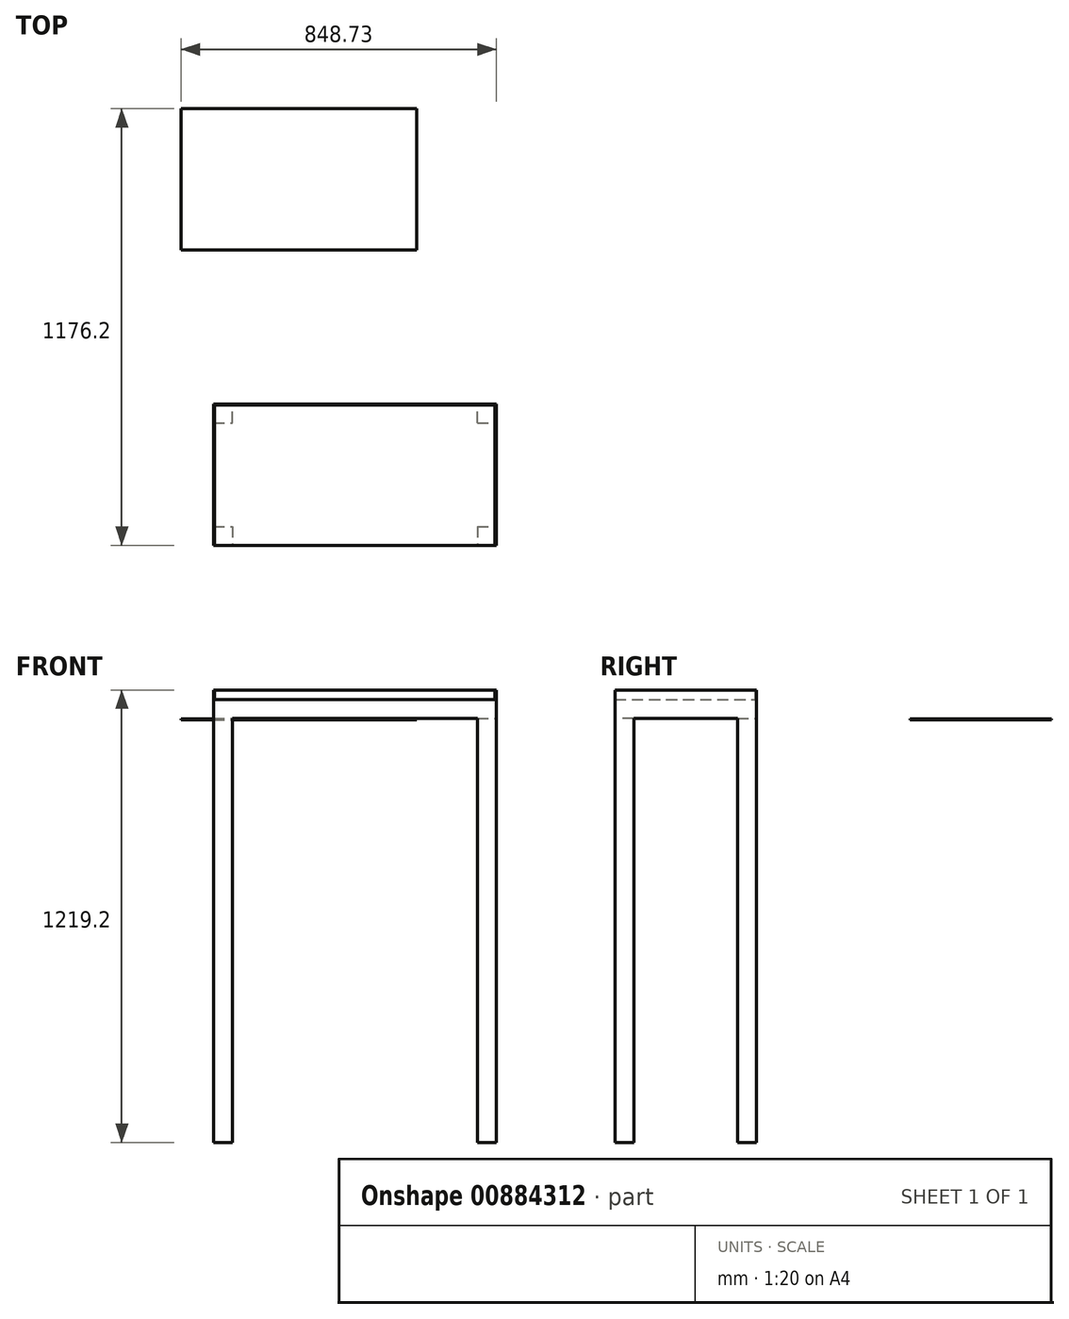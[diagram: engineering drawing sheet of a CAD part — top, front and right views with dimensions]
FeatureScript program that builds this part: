
annotation { "Feature Type Name" : "Feature", "Feature Type Description" : "" }
export const myFeature = defineFeature(function(context is Context, id is Id, definition is map)
    precondition{}
    {
        {
            var Q0;
            Q0=qCreatedBy(makeId("Front.planeOp"),FACE);
            var sketch = newSketch(context, id + "F0", { "sketchPlane" : qUnion([Q0])});
            skLineSegment(sketch, "E0.bottom", {"start": v(-294.8, 52.32) * mm, "end": v(467.2, 52.32) * mm});
            skLineSegment(sketch, "E0.top", {"start": v(-294.8, 1.52) * mm, "end": v(467.2, 1.52) * mm});
            skLineSegment(sketch, "E0.left", {"start": v(-294.8, 52.32) * mm, "end": v(-294.8, 1.52) * mm});
            skLineSegment(sketch, "E0.right", {"start": v(467.2, 52.32) * mm, "end": v(467.2, 1.52) * mm});
            skSolve(sketch);
        }
        {
            var Q0;
            Q0=makeQuery(id+"F0.imprint","IMPRINT",FACE,{"disambiguationData":[TD([[makeQuery(id+"F0.imprint","IMPRINT",EDGE,{"derivedFrom":sQuery(id+"F0.wireOp",EDGE,"E0.bottom")}),-1.0]])]});
            extrude(context, id + "F1", {"entities" : qUnion([Q0]), "depth" : 381 * mm, "offsetDistance" : 25.4 * mm});
        }
        {
            var Q0;
            Q0=makeQuery(id+"F1.opExtrude","CAP_FACE",FACE,{"disambiguationData":[OSD([sQuery(id+"F0.wireOp",EDGE,"E0.bottom"),sQuery(id+"F0.wireOp",EDGE,"E0.top"),sQuery(id+"F0.wireOp",EDGE,"E0.left"),sQuery(id+"F0.wireOp",EDGE,"E0.right")])],"isStart":false});
            var sketch = newSketch(context, id + "F2", { "sketchPlane" : qUnion([Q0])});
            skLineSegment(sketch, "E1", {"start": v(-294.8, 1.52) * mm, "end": v(-294.8, -1141.48) * mm});
            skLineSegment(sketch, "E2", {"start": v(-294.8, -1141.48) * mm, "end": v(-244, -1141.48) * mm});
            skLineSegment(sketch, "E3", {"start": v(-244, -1141.48) * mm, "end": v(-244, 1.52) * mm});
            skLineSegment(sketch, "E4", {"start": v(467.2, 1.52) * mm, "end": v(467.2, -1141.48) * mm});
            skLineSegment(sketch, "E5", {"start": v(467.2, -1141.48) * mm, "end": v(416.4, -1141.48) * mm});
            skLineSegment(sketch, "E6", {"start": v(416.4, -1141.48) * mm, "end": v(416.4, 1.52) * mm});
            skSolve(sketch);
        }
        {
            var Q0;
            {var subQ0=sQuery(id+"F2.wireOp",EDGE,"E1");Q0=makeQuery(id+"F2.imprint","IMPRINT",FACE,{"disambiguationData":[TD([[makeQuery(id+"F2.imprint","IMPRINT",EDGE,{"derivedFrom":subQ0}),1.0]])]});}
            var Q1;
            {var subQ0=sQuery(id+"F2.wireOp",EDGE,"E4");Q1=makeQuery(id+"F2.imprint","IMPRINT",FACE,{"disambiguationData":[TD([[makeQuery(id+"F2.imprint","IMPRINT",EDGE,{"derivedFrom":subQ0}),-1.0]])]});}
            extrude(context, id + "F3", {"entities" : qUnion([Q0, Q1]), "operationType" : NewBodyOperationType.ADD, "depth" : -50.8 * mm, "offsetDistance" : 25.4 * mm});
        }
        {
            var Q0;
            Q0=makeQuery(id+"F1.opExtrude","CAP_FACE",FACE,{"disambiguationData":[OSD([sQuery(id+"F0.wireOp",EDGE,"E0.bottom"),sQuery(id+"F0.wireOp",EDGE,"E0.top"),sQuery(id+"F0.wireOp",EDGE,"E0.left"),sQuery(id+"F0.wireOp",EDGE,"E0.right")])],"isStart":true});
            var sketch = newSketch(context, id + "F4", { "sketchPlane" : qUnion([Q0])});
            skLineSegment(sketch, "E7", {"start": v(-467.2, 1.52) * mm, "end": v(-467.2, -1141.48) * mm});
            skLineSegment(sketch, "E8", {"start": v(-467.2, -1141.48) * mm, "end": v(-416.4, -1141.48) * mm});
            skLineSegment(sketch, "E9", {"start": v(-416.4, -1141.48) * mm, "end": v(-416.4, 1.52) * mm});
            skLineSegment(sketch, "E10", {"start": v(294.8, 1.52) * mm, "end": v(294.8, -1141.48) * mm});
            skLineSegment(sketch, "E11", {"start": v(294.8, -1141.48) * mm, "end": v(244, -1141.48) * mm});
            skLineSegment(sketch, "E12", {"start": v(244, -1141.48) * mm, "end": v(244, 1.52) * mm});
            skSolve(sketch);
        }
        {
            var Q0;
            {var subQ0=sQuery(id+"F4.wireOp",EDGE,"E7");Q0=makeQuery(id+"F4.imprint","IMPRINT",FACE,{"disambiguationData":[TD([[makeQuery(id+"F4.imprint","IMPRINT",EDGE,{"derivedFrom":subQ0}),1.0]])]});}
            var Q1;
            {var subQ0=sQuery(id+"F4.wireOp",EDGE,"E10");Q1=makeQuery(id+"F4.imprint","IMPRINT",FACE,{"disambiguationData":[TD([[makeQuery(id+"F4.imprint","IMPRINT",EDGE,{"derivedFrom":subQ0}),-1.0]])]});}
            extrude(context, id + "F5", {"entities" : qUnion([Q0, Q1]), "operationType" : NewBodyOperationType.ADD, "depth" : -50.8 * mm, "offsetDistance" : 25.4 * mm});
        }
        {
            var Q0;
            Q0=makeQuery(id+"F5.boolean.opBoolean","MERGE",FACE,{"derivedFrom":[makeQuery(id+"F3.boolean.opBoolean","MERGE",FACE,{"derivedFrom":[makeQuery(id+"F1.opExtrude","SWEPT_FACE",FACE,{"disambiguationData":[OSD([sQuery(id+"F0.wireOp",EDGE,"E0.right")])]}),makeQuery(id+"F3.opExtrude","SWEPT_FACE",FACE,{"disambiguationData":[OSD([sQuery(id+"F2.wireOp",EDGE,"E4")])]})]}),makeQuery(id+"F5.opExtrude","SWEPT_FACE",FACE,{"disambiguationData":[OSD([sQuery(id+"F4.wireOp",EDGE,"E7")])]})]});
            var sketch = newSketch(context, id + "F6", { "sketchPlane" : qUnion([Q0])});
            skLineSegment(sketch, "E13", {"start": v(-381, 52.32) * mm, "end": v(-381, 77.72) * mm});
            skLineSegment(sketch, "E14", {"start": v(-381, 77.72) * mm, "end": v(0, 77.72) * mm});
            skLineSegment(sketch, "E15", {"start": v(0, 77.72) * mm, "end": v(0, 52.32) * mm});
            skLineSegment(sketch, "E16", {"start": v(0, 52.32) * mm, "end": v(-381, 52.32) * mm});
            skSolve(sketch);
        }
        {
            var Q0;
            Q0=makeQuery(id+"F6.imprint","IMPRINT",FACE,{"disambiguationData":[TD([[makeQuery(id+"F6.imprint","IMPRINT",EDGE,{"derivedFrom":sQuery(id+"F6.wireOp",EDGE,"E13")}),-1.0]])]});
            extrude(context, id + "F7", {"entities" : qUnion([Q0]), "operationType" : NewBodyOperationType.ADD, "depth" : -3.17 * mm, "offsetDistance" : 25.4 * mm});
        }
        {
            var Q0;
            {var subQ0=sQuery(id+"F0.wireOp",EDGE,"E0.top");Q0=makeQuery(id+"F7.boolean.opBoolean","MERGE",FACE,{"derivedFrom":[makeQuery(id+"F5.boolean.opBoolean","MERGE",FACE,{"derivedFrom":[makeQuery(id+"F1.opExtrude","CAP_FACE",FACE,{"disambiguationData":[OSD([sQuery(id+"F0.wireOp",EDGE,"E0.bottom"),subQ0,sQuery(id+"F0.wireOp",EDGE,"E0.left"),sQuery(id+"F0.wireOp",EDGE,"E0.right")])],"isStart":true}),makeQuery(id+"F5.opExtrude","CAP_FACE",FACE,{"disambiguationData":[OSD([subQ0,sQuery(id+"F4.wireOp",EDGE,"E7"),sQuery(id+"F4.wireOp",EDGE,"E8"),sQuery(id+"F4.wireOp",EDGE,"E9")])],"isStart":true}),makeQuery(id+"F5.opExtrude","CAP_FACE",FACE,{"disambiguationData":[OSD([subQ0,sQuery(id+"F4.wireOp",EDGE,"E10"),sQuery(id+"F4.wireOp",EDGE,"E11"),sQuery(id+"F4.wireOp",EDGE,"E12")])],"isStart":true})]}),makeQuery(id+"F7.opExtrude","SWEPT_FACE",FACE,{"disambiguationData":[OSD([sQuery(id+"F6.wireOp",EDGE,"E15")])]})]});}
            var sketch = newSketch(context, id + "F8", { "sketchPlane" : qUnion([Q0])});
            skLineSegment(sketch, "E17", {"start": v(-467.2, 77.72) * mm, "end": v(294.8, 77.72) * mm});
            skLineSegment(sketch, "E18", {"start": v(294.8, 77.72) * mm, "end": v(294.8, 52.32) * mm});
            skLineSegment(sketch, "E19", {"start": v(294.8, 52.32) * mm, "end": v(-467.2, 52.32) * mm});
            skLineSegment(sketch, "E20", {"start": v(-467.2, 52.32) * mm, "end": v(-467.2, 77.72) * mm});
            skSolve(sketch);
        }
        {
            var Q0;
            {var subQ0=sQuery(id+"F8.wireOp",EDGE,"E20");Q0=makeQuery(id+"F8.imprint","IMPRINT",FACE,{"disambiguationData":[TD([[makeQuery(id+"F8.imprint","IMPRINT",EDGE,{"derivedFrom":subQ0}),1.0]])]});}
            extrude(context, id + "F9", {"entities" : qUnion([Q0]), "operationType" : NewBodyOperationType.ADD, "depth" : -3.17 * mm, "offsetDistance" : 25.4 * mm});
        }
        {
            var Q0;
            {var subQ0=sQuery(id+"F0.wireOp",EDGE,"E0.top");Q0=makeQuery(id+"F7.boolean.opBoolean","MERGE",FACE,{"derivedFrom":[makeQuery(id+"F5.boolean.opBoolean","MERGE",FACE,{"derivedFrom":[makeQuery(id+"F1.opExtrude","CAP_FACE",FACE,{"disambiguationData":[OSD([sQuery(id+"F0.wireOp",EDGE,"E0.bottom"),subQ0,sQuery(id+"F0.wireOp",EDGE,"E0.left"),sQuery(id+"F0.wireOp",EDGE,"E0.right")])],"isStart":true}),makeQuery(id+"F5.opExtrude","CAP_FACE",FACE,{"disambiguationData":[OSD([subQ0,sQuery(id+"F4.wireOp",EDGE,"E7"),sQuery(id+"F4.wireOp",EDGE,"E8"),sQuery(id+"F4.wireOp",EDGE,"E9")])],"isStart":true}),makeQuery(id+"F5.opExtrude","CAP_FACE",FACE,{"disambiguationData":[OSD([subQ0,sQuery(id+"F4.wireOp",EDGE,"E10"),sQuery(id+"F4.wireOp",EDGE,"E11"),sQuery(id+"F4.wireOp",EDGE,"E12")])],"isStart":true})]}),makeQuery(id+"F7.opExtrude","SWEPT_FACE",FACE,{"disambiguationData":[OSD([sQuery(id+"F6.wireOp",EDGE,"E15")])]})]});}
            var sketch = newSketch(context, id + "F10", { "sketchPlane" : qUnion([Q0])});
            skLineSegment(sketch, "E21", {"start": v(-464.03, 77.72) * mm, "end": v(291.62, 77.72) * mm});
            skLineSegment(sketch, "E22", {"start": v(291.62, 77.72) * mm, "end": v(291.62, 52.32) * mm});
            skLineSegment(sketch, "E23", {"start": v(291.62, 52.32) * mm, "end": v(-464.03, 52.32) * mm});
            skLineSegment(sketch, "E24", {"start": v(-464.03, 52.32) * mm, "end": v(-464.03, 77.72) * mm});
            skSolve(sketch);
        }
        {
            var Q0;
            Q0=makeQuery(id+"F10.imprint","IMPRINT",FACE,{"disambiguationData":[TD([[makeQuery(id+"F10.imprint","IMPRINT",EDGE,{"derivedFrom":sQuery(id+"F10.wireOp",EDGE,"E21")}),-1.0]])]});
            extrude(context, id + "F11", {"entities" : qUnion([Q0]), "operationType" : NewBodyOperationType.ADD, "depth" : -3.17 * mm, "offsetDistance" : 25.4 * mm});
        }
        {
            var Q0;
            Q0=makeQuery(id+"F5.boolean.opBoolean","MERGE",FACE,{"derivedFrom":[makeQuery(id+"F3.boolean.opBoolean","MERGE",FACE,{"derivedFrom":[makeQuery(id+"F1.opExtrude","SWEPT_FACE",FACE,{"disambiguationData":[OSD([sQuery(id+"F0.wireOp",EDGE,"E0.left")])]}),makeQuery(id+"F3.opExtrude","SWEPT_FACE",FACE,{"disambiguationData":[OSD([sQuery(id+"F2.wireOp",EDGE,"E1")])]})]}),makeQuery(id+"F5.opExtrude","SWEPT_FACE",FACE,{"disambiguationData":[OSD([sQuery(id+"F4.wireOp",EDGE,"E10")])]})]});
            var sketch = newSketch(context, id + "F12", { "sketchPlane" : qUnion([Q0])});
            skLineSegment(sketch, "E25", {"start": v(381, 52.32) * mm, "end": v(3.18, 52.32) * mm});
            skLineSegment(sketch, "E26", {"start": v(3.18, 52.32) * mm, "end": v(3.18, 77.72) * mm});
            skLineSegment(sketch, "E27", {"start": v(3.18, 77.72) * mm, "end": v(381, 77.72) * mm});
            skLineSegment(sketch, "E28", {"start": v(381, 77.72) * mm, "end": v(381, 52.32) * mm});
            skSolve(sketch);
        }
        {
            var Q0;
            Q0=makeQuery(id+"F12.imprint","IMPRINT",FACE,{"disambiguationData":[TD([[makeQuery(id+"F12.imprint","IMPRINT",EDGE,{"derivedFrom":sQuery(id+"F12.wireOp",EDGE,"E25")}),-1.0]])]});
            extrude(context, id + "F13", {"entities" : qUnion([Q0]), "operationType" : NewBodyOperationType.ADD, "depth" : -3.17 * mm, "offsetDistance" : 25.4 * mm});
        }
        {
            var Q0;
            Q0=makeQuery(id+"F7.opExtrude","CAP_FACE",FACE,{"disambiguationData":[OSD([sQuery(id+"F6.wireOp",EDGE,"E13"),sQuery(id+"F6.wireOp",EDGE,"E14"),sQuery(id+"F6.wireOp",EDGE,"E15"),sQuery(id+"F6.wireOp",EDGE,"E16")])],"isStart":false});
            extrude(context, id + "F14", {"entities" : qUnion([Q0]), "operationType" : NewBodyOperationType.ADD, "depth" : -3.17 * mm, "offsetDistance" : 25.4 * mm});
        }
        {
            var Q0;
            Q0=makeQuery(id+"F11.opExtrude","SWEPT_FACE",FACE,{"disambiguationData":[OSD([sQuery(id+"F10.wireOp",EDGE,"E22")])]});
            var sketch = newSketch(context, id + "F15", { "sketchPlane" : qUnion([Q0])});
            skLineSegment(sketch, "E29", {"start": v(0, 77.72) * mm, "end": v(381, 77.72) * mm});
            skLineSegment(sketch, "E30", {"start": v(381, 77.72) * mm, "end": v(381, 52.32) * mm});
            skLineSegment(sketch, "E31", {"start": v(381, 52.32) * mm, "end": v(0, 52.32) * mm});
            skLineSegment(sketch, "E32", {"start": v(0, 52.32) * mm, "end": v(0, 77.72) * mm});
            skSolve(sketch);
        }
        {
            var Q0;
            Q0=makeQuery(id+"F5.boolean.opBoolean","MERGE",FACE,{"derivedFrom":[makeQuery(id+"F3.boolean.opBoolean","MERGE",FACE,{"derivedFrom":[makeQuery(id+"F1.opExtrude","SWEPT_FACE",FACE,{"disambiguationData":[OSD([sQuery(id+"F0.wireOp",EDGE,"E0.left")])]}),makeQuery(id+"F3.opExtrude","SWEPT_FACE",FACE,{"disambiguationData":[OSD([sQuery(id+"F2.wireOp",EDGE,"E1")])]})]}),makeQuery(id+"F5.opExtrude","SWEPT_FACE",FACE,{"disambiguationData":[OSD([sQuery(id+"F4.wireOp",EDGE,"E10")])]})]});
            var sketch = newSketch(context, id + "F16", { "sketchPlane" : qUnion([Q0])});
            skLineSegment(sketch, "E33", {"start": v(0, 52.32) * mm, "end": v(0, 77.72) * mm});
            skLineSegment(sketch, "E34", {"start": v(0, 77.72) * mm, "end": v(381, 77.72) * mm});
            skLineSegment(sketch, "E35", {"start": v(381, 77.72) * mm, "end": v(381, 52.32) * mm});
            skLineSegment(sketch, "E36", {"start": v(381, 52.32) * mm, "end": v(0, 52.32) * mm});
            skSolve(sketch);
        }
        {
            var Q0;
            Q0=makeQuery(id+"F16.imprint","IMPRINT",FACE,{"disambiguationData":[TD([[makeQuery(id+"F16.imprint","IMPRINT",EDGE,{"derivedFrom":sQuery(id+"F16.wireOp",EDGE,"E33")}),-1.0]])]});
            extrude(context, id + "F17", {"entities" : qUnion([Q0]), "operationType" : NewBodyOperationType.ADD, "depth" : -3.17 * mm, "offsetDistance" : 25.4 * mm});
        }
        {
            var Q0;
            Q0=qCreatedBy(makeId("Top.planeOp"), FACE);
            var sketch = newSketch(context, id + "F18", { "sketchPlane" : qUnion([Q0])});
            skLineSegment(sketch, "E37.bottom", {"start": v(-381.53, 795.2) * mm, "end": v(253.47, 795.2) * mm});
            skLineSegment(sketch, "E37.top", {"start": v(-381.53, 414.2) * mm, "end": v(253.47, 414.2) * mm});
            skLineSegment(sketch, "E37.left", {"start": v(-381.53, 795.2) * mm, "end": v(-381.53, 414.2) * mm});
            skLineSegment(sketch, "E37.right", {"start": v(253.47, 795.2) * mm, "end": v(253.47, 414.2) * mm});
            skSolve(sketch);
        }
        {
            var Q0;
            Q0 = qSketchRegion(id + "F18", true);
            extrude(context, id + "F19", {"entities" : qUnion([Q0]), "domain" : OperationDomain.MODEL, "flatOperationType" : FlatOperationType.REMOVE, "oppositeDirection" : true, "depth" : 3.17 * mm, "offsetDistance" : 25.4 * mm});
        }
    });
